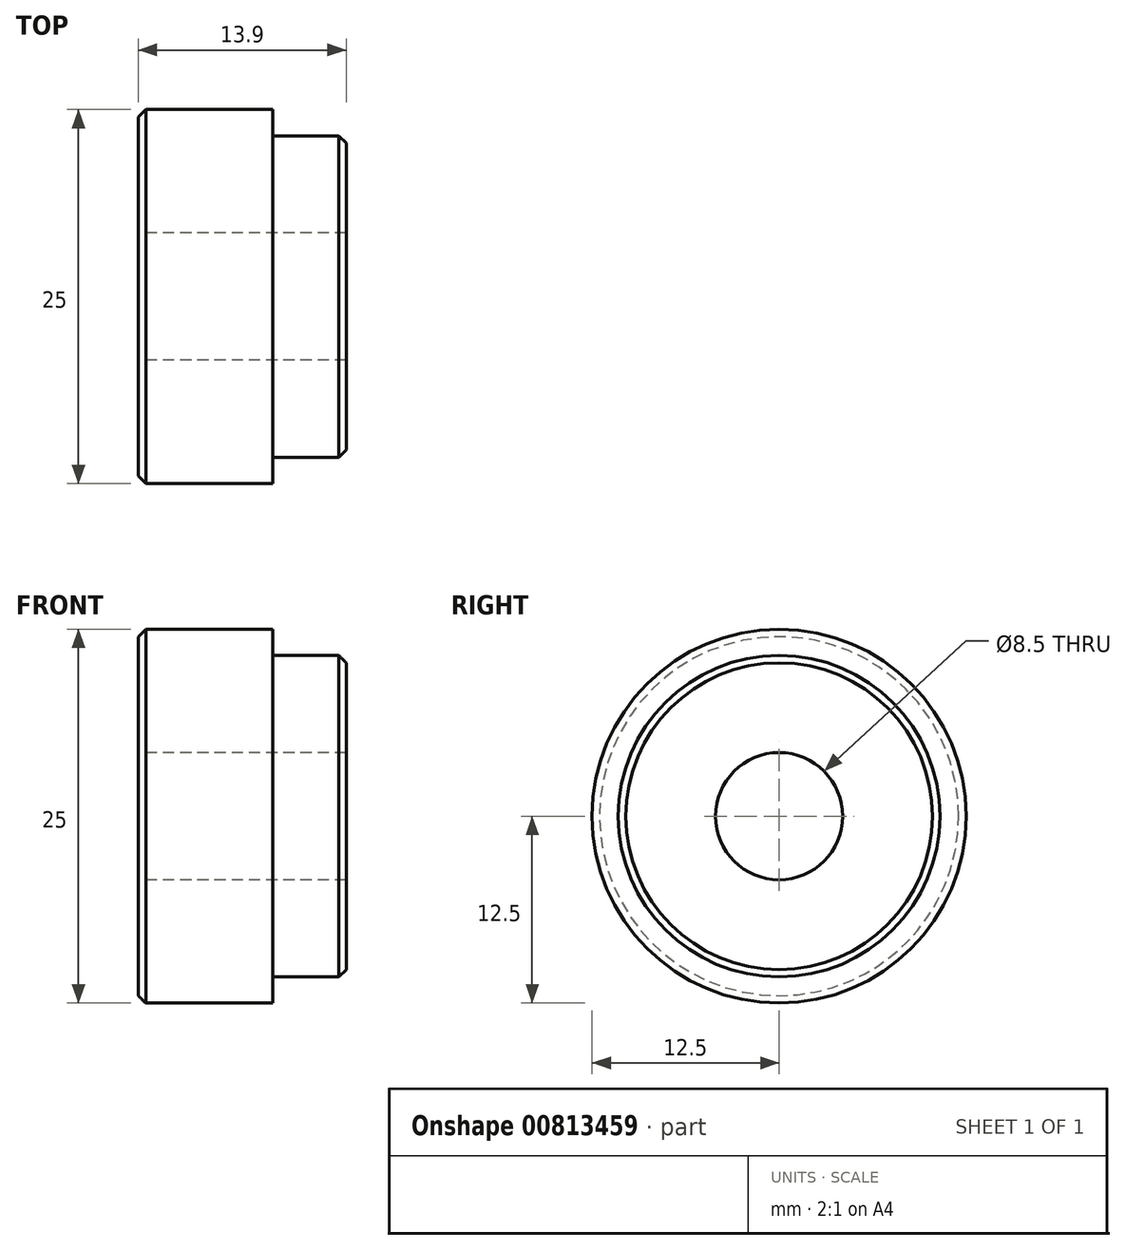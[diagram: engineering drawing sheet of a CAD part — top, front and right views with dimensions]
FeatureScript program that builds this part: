
annotation { "Feature Type Name" : "Feature", "Feature Type Description" : "" }
export const myFeature = defineFeature(function(context is Context, id is Id, definition is map)
    precondition{}
    {
        {
            var Q0;
            Q0=qCreatedBy(makeId("Front.planeOp"),FACE);
            var sketch = newSketch(context, id + "F0", { "sketchPlane" : qUnion([Q0])});
            skLineSegment(sketch, "E0", {"start": v(0, 0) * mm, "end": v(13.9, 0) * mm});
            skLineSegment(sketch, "E1", {"start": v(13.9, 0) * mm, "end": v(13.9, 10.75) * mm});
            skLineSegment(sketch, "E2", {"start": v(13.9, 10.75) * mm, "end": v(9, 10.75) * mm});
            skLineSegment(sketch, "E3", {"start": v(9, 10.75) * mm, "end": v(9, 12.5) * mm});
            skLineSegment(sketch, "E4", {"start": v(9, 12.5) * mm, "end": v(0, 12.5) * mm});
            skLineSegment(sketch, "E5", {"start": v(0, 12.5) * mm, "end": v(0, 0) * mm});
            skLineSegment(sketch, "E6", {"start": v(0, 0) * mm, "end": v(23.56, 0) * mm, "construction": true});
            skPoint(sketch, "E7", {"position": v(13.9, 0) * mm});
            skSolve(sketch);
        }
        {
            var Q0;
            Q0=makeQuery(id+"F0.imprint","IMPRINT",FACE,{"disambiguationData":[TD([[makeQuery(id+"F0.imprint","IMPRINT",EDGE,{"derivedFrom":sQuery(id+"F0.wireOp",EDGE,"E0")}),1.0]])]});
            var Q1;
            Q1=sQuery(id+"F0.wireOp",EDGE,"E0");
            revolve(context, id + "F1", {"surfaceOperationType" : NewSurfaceOperationType.NEW, "entities" : qUnion([Q0]), "axis" : qUnion([Q1]), "revolveType" : RevolveType.FULL});
        }
        {
            var Q0;
            Q0=makeQuery(id+"F1.opRevolve","SWEPT_FACE",FACE,{"disambiguationData":[OSD([sQuery(id+"F0.wireOp",EDGE,"E5")])]});
            var sketch = newSketch(context, id + "F2", { "sketchPlane" : qUnion([Q0])});
            skCircle(sketch, "E8", {"center": v(0, 0) * mm, "radius": 4.25 * mm});
            skSolve(sketch);
        }
        {
            var Q0;
            Q0=makeQuery(id+"F2.imprint","IMPRINT",FACE,{"disambiguationData":[TD([[makeQuery(id+"F2.imprint","IMPRINT",EDGE,{"derivedFrom":sQuery(id+"F2.wireOp",EDGE,"E8")}),1.0]])]});
            extrude(context, id + "F3", {"entities" : qUnion([Q0]), "operationType" : NewBodyOperationType.REMOVE, "endBound" : BoundingType.UP_TO_NEXT, "oppositeDirection" : true, "depth" : 25 * mm, "offsetDistance" : 25 * mm});
        }
        {
            var Q0;
            Q0=makeQuery(id+"F1.opRevolve","SWEPT_EDGE",EDGE,{"disambiguationData":[OSD([sQuery(id+"F0.wireOp",EDGE,"E1"),sQuery(id+"F0.wireOp",EDGE,"E2")])]});
            var Q1;
            Q1=makeQuery(id+"F1.opRevolve","SWEPT_EDGE",EDGE,{"disambiguationData":[OSD([sQuery(id+"F0.wireOp",EDGE,"E4"),sQuery(id+"F0.wireOp",EDGE,"E5")])]});
            chamfer(context, id + "F4", {"entities" : qUnion([Q0, Q1]), "width" : 0.5 * mm, "tangentPropagation" : true});
        }
    });
